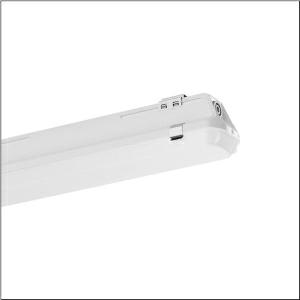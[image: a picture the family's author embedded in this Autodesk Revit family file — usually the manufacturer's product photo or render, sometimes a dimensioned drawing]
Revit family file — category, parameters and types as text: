
# Revit family: monsun_r__21_51fb107p460b_c23d
name_source: partatom
category: Lighting Fixtures
units: mm (PartAtom-declared; Revit-internal decimal feet)

## family parameters
Cut with Voids When Loaded = No
Host = Face
Light Source = No
Part Type = Normal
Room Calculation Point = No
Round Connector Dimension = Use Diameter
Shared = No

## types (1)
- Monsun® 21 (1 x LED, 6000 lm, 38 W, 4000K)
    Apparent Load = 38 VA
    CIE Flux Codes = 47 77 93 94 100
    Color Rendering = 80
    Color Temperature = 4000K
    Default Elevation = 1800 mm
    Description = Monsun® 21, damp-proof luminaire, chain hanger, primary optical cover: enclosure, of PMMA, light emission: direct distribution, primary light characteristic: symmetric, installation type: suspended mounting, surface-mounted, horizontal mounting, vertical mounting, LED, rated luminous flux: 6.000lm, luminous efficacy: 158lm/W, light colour: 840, colour temperature: 4000K, control gear: ECG, with terminal, 3-pole, max. 2.5mm², mains connection: 220..240V, AC, 50/60Hz, rated input power: 38W, housing, of glass-fibre reinforced polyester, uncoated, bright grey, incl. chain hanger, length: 1.590mm, width: 90mm, height: 88mm, clip for enclosure, of stainless steel (V2A), ceiling mounting element, of stainless steel (V2A), chain hanger, of stainless steel (V2A), protection rating (complete): IP66, insulation class (complete): insulation class I (protective earthing), certification: CE, ENEC, VDE, UKCA, protection symbol: D, impact resistance: IK04, permissible operating ambient temperature: -25..+35°C, standard: EN 50419, EN 60598-2-1, corresponds to IFS (International Featured Standards) requirements for safety and quality in the food industry, for indoor or canopied outdoor use, no direct snow, no direct sun, no direct rain, contact your sales advisor before using the luminaires in applications with unclear chemical exposure, large temperature fluctuations or condensation-forming humidity, LABS conformity tested according to VDMA 24364:2018-05, packaging unit: 1 piece
    Height = 89 mm
    Lamp = 1 x LED
    Lamp Light Flux = 6000 lm
    Lamp Power = 38 W
    Lamp count = 1
    Length = 1590 mm
    Luminous efficacy = 158 lm/W
    Manufacturer = Siteco
    ModVariant = No
    Model = 51FB107P460B
    Mounting Place = Ceiling
    Mounting Type = Surface mounted
    Number of Poles = 1
    OnlyDefault = Yes
    Power Factor = 1
    Product Name = Monsun® 21
    Product group = damp-proof luminaire
    ProductGroupID = 301
    Protection Class = Protection class I
    Protection Degree = IP 66
    RLX_Detail_Level = 1
    RLX_Emergency_Light_Flux = 0 lm
    RLX_Emergency_Type = 0
    RLX_Emergency_Type_DB = No
    RlxData = <blob elided: 88549 chars, md5=7fb0ad4d>
    Socket = socket
    Standby Power = 0 W
    System Light Flux = 6000 lm
    System Power = 38 W
    Type Comments = Product without accessories
    Type Image = l_1006717.jpg
    URL = http://relux.com
    VarID = ---
    Voltage = 0 V
    Weight = 0.00 kg
    Width = 90 mm

## geometry (parser evidence)
native form markers: Blend x4, Sweep x15
no freeform markers — native parametric forms only
